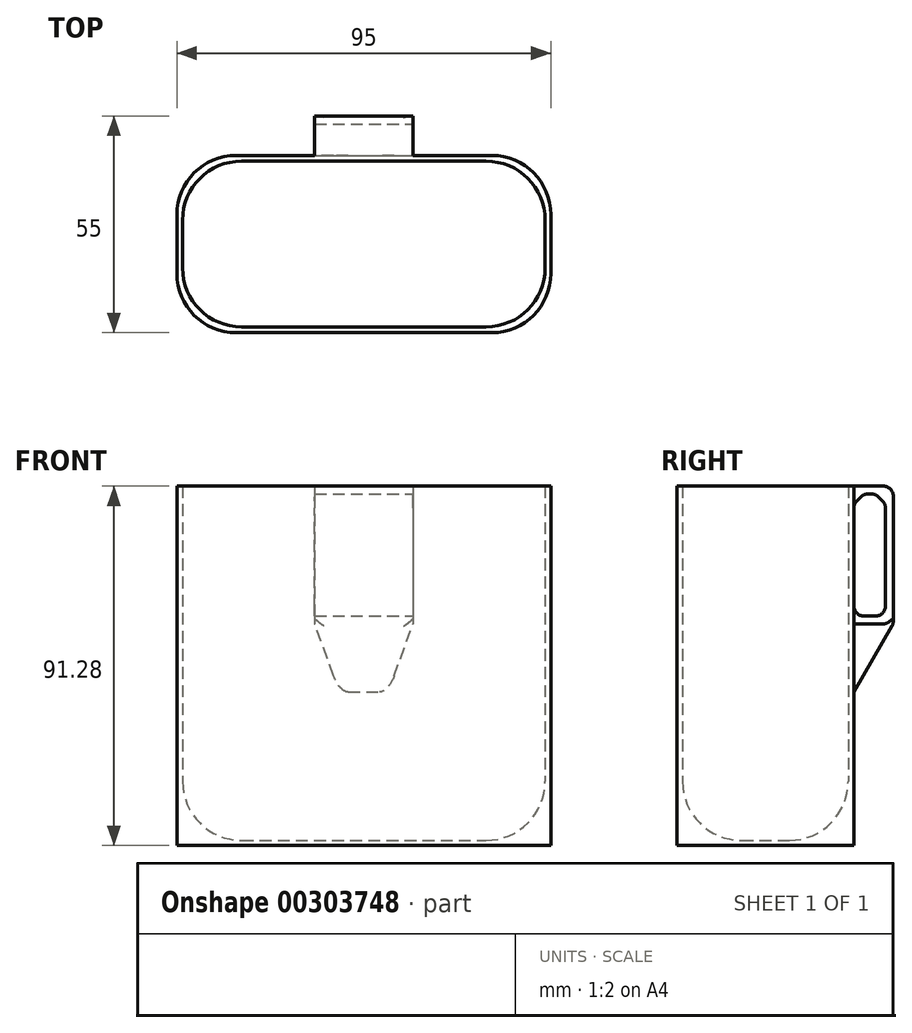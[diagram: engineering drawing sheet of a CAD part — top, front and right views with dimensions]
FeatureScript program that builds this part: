
annotation { "Feature Type Name" : "Feature", "Feature Type Description" : "" }
export const myFeature = defineFeature(function(context is Context, id is Id, definition is map)
    precondition{}
    {
        {
            var Q0;
            Q0=qCreatedBy(makeId("Top.planeOp"),FACE);
            var sketch = newSketch(context, id + "F0", { "sketchPlane" : qUnion([Q0])});
            skLineSegment(sketch, "E0.bottom", {"start": v(0, 0) * mm, "end": v(95, 0) * mm});
            skLineSegment(sketch, "E0.top", {"start": v(0, 45) * mm, "end": v(95, 45) * mm});
            skLineSegment(sketch, "E0.left", {"start": v(0, 0) * mm, "end": v(0, 45) * mm});
            skLineSegment(sketch, "E0.right", {"start": v(95, 0) * mm, "end": v(95, 45) * mm});
            skSolve(sketch);
        }
        {
            var Q0;
            Q0 = qSketchRegion(id + "F0", true);
            extrude(context, id + "F1", {"entities" : qUnion([Q0]), "depth" : (.32 * 4) * mm});
        }
        {
            var Q0;
            Q0=makeQuery(id+"F1.opExtrude","CAP_FACE",FACE,{"disambiguationData":[OSD([sQuery(id+"F0.wireOp",EDGE,"E0.bottom"),sQuery(id+"F0.wireOp",EDGE,"E0.top"),sQuery(id+"F0.wireOp",EDGE,"E0.left"),sQuery(id+"F0.wireOp",EDGE,"E0.right")])],"isStart":false});
            var sketch = newSketch(context, id + "F2", { "sketchPlane" : qUnion([Q0])});
            skLineSegment(sketch, "E1.0.0", {"start": v(95, 45) * mm, "end": v(0, 45) * mm});
            skLineSegment(sketch, "E1.0.1", {"start": v(0, 45) * mm, "end": v(0, 0) * mm});
            skLineSegment(sketch, "E1.0.2", {"start": v(0, 0) * mm, "end": v(95, 0) * mm});
            skLineSegment(sketch, "E1.0.3", {"start": v(95, 0) * mm, "end": v(95, 45) * mm});
            skLineSegment(sketch, "E2.0", {"start": v(93.56, 43.56) * mm, "end": v(1.44, 43.56) * mm});
            skLineSegment(sketch, "E2.1", {"start": v(93.56, 1.44) * mm, "end": v(93.56, 43.56) * mm});
            skLineSegment(sketch, "E2.2", {"start": v(1.44, 1.44) * mm, "end": v(93.56, 1.44) * mm});
            skLineSegment(sketch, "E2.3", {"start": v(1.44, 43.56) * mm, "end": v(1.44, 1.44) * mm});
            skSolve(sketch);
        }
        {
            var Q0;
            Q0 = qSketchRegion(id + "F2", true);
            extrude(context, id + "F3", {"entities" : qUnion([Q0]), "operationType" : NewBodyOperationType.ADD, "depth" : 90 * mm});
        }
        {
            var Q0;
            Q0=makeQuery(id+"F3.boolean.opBoolean","MERGE",FACE,{"derivedFrom":[makeQuery(id+"F1.opExtrude","SWEPT_FACE",FACE,{"disambiguationData":[OSD([sQuery(id+"F0.wireOp",EDGE,"E0.top")])]}),makeQuery(id+"F3.opExtrude","SWEPT_FACE",FACE,{"disambiguationData":[OSD([sQuery(id+"F2.wireOp",EDGE,"E1.0.0")])]})]});
            var sketch = newSketch(context, id + "F4", { "sketchPlane" : qUnion([Q0])});
            skLineSegment(sketch, "E3.bottom", {"start": v(-60, 91.28) * mm, "end": v(-35, 91.28) * mm});
            skLineSegment(sketch, "E3.top", {"start": v(-60, 56.28) * mm, "end": v(-35, 56.28) * mm});
            skLineSegment(sketch, "E3.left", {"start": v(-60, 91.28) * mm, "end": v(-60, 56.28) * mm});
            skLineSegment(sketch, "E3.right", {"start": v(-35, 91.28) * mm, "end": v(-35, 56.28) * mm});
            skSolve(sketch);
        }
        {
            var Q0;
            Q0 = qSketchRegion(id + "F4", true);
            extrude(context, id + "F5", {"entities" : qUnion([Q0]), "operationType" : NewBodyOperationType.ADD, "depth" : 10 * mm});
        }
        {
            var Q0;
            Q0=makeQuery(id+"F5.opExtrude","SWEPT_FACE",FACE,{"disambiguationData":[OSD([sQuery(id+"F4.wireOp",EDGE,"E3.left")])]});
            var sketch = newSketch(context, id + "F6", { "sketchPlane" : qUnion([Q0])});
            skLineSegment(sketch, "E4.0", {"start": v(53, 89.28) * mm, "end": v(45, 89.28) * mm});
            skLineSegment(sketch, "E4.1", {"start": v(53, 89.28) * mm, "end": v(53, 58.28) * mm});
            skLineSegment(sketch, "E4.2", {"start": v(53, 58.28) * mm, "end": v(45, 58.28) * mm});
            skLineSegment(sketch, "E5", {"start": v(45, 89.28) * mm, "end": v(45, 58.28) * mm});
            skSolve(sketch);
        }
        {
            var Q0;
            Q0 = qSketchRegion(id + "F6", true);
            extrude(context, id + "F7", {"entities" : qUnion([Q0]), "operationType" : NewBodyOperationType.REMOVE, "endBound" : BoundingType.THROUGH_ALL, "oppositeDirection" : true, "depth" : 25 * mm});
        }
        {
            var Q0;
            Q0=makeQuery(id+"F5.opExtrude","SWEPT_FACE",FACE,{"disambiguationData":[OSD([sQuery(id+"F4.wireOp",EDGE,"E3.left")])]});
            var sketch = newSketch(context, id + "F8", { "sketchPlane" : qUnion([Q0])});
            skLineSegment(sketch, "E6", {"start": v(45, 56.28) * mm, "end": v(55, 56.28) * mm});
            skLineSegment(sketch, "E7", {"start": v(55, 56.28) * mm, "end": v(45, 38.96) * mm});
            skLineSegment(sketch, "E8", {"start": v(45, 56.28) * mm, "end": v(45, 38.96) * mm});
            skSolve(sketch);
        }
        {
            var Q0;
            Q0 = qSketchRegion(id + "F8", true);
            var Q1;
            Q1=makeQuery(id+"F5.opExtrude","SWEPT_FACE",FACE,{"disambiguationData":[OSD([sQuery(id+"F4.wireOp",EDGE,"E3.right")])]});
            extrude(context, id + "F9", {"entities" : qUnion([Q0]), "operationType" : NewBodyOperationType.ADD, "endBound" : BoundingType.UP_TO_SURFACE, "oppositeDirection" : true, "endBoundEntityFace" : qUnion([Q1]), "depth" : 25 * mm});
        }
        {
            var Q0;
            Q0=makeQuery(id+"F5.opExtrude","CAP_FACE",FACE,{"disambiguationData":[OSD([sQuery(id+"F4.wireOp",EDGE,"E3.bottom"),sQuery(id+"F4.wireOp",EDGE,"E3.top"),sQuery(id+"F4.wireOp",EDGE,"E3.left"),sQuery(id+"F4.wireOp",EDGE,"E3.right")])],"isStart":false});
            var sketch = newSketch(context, id + "F10", { "sketchPlane" : qUnion([Q0])});
            skLineSegment(sketch, "E9.0.2", {"start": v(-60, 56.28) * mm, "end": v(-60, 38.96) * mm});
            skLineSegment(sketch, "E9.0.3", {"start": v(-60, 38.96) * mm, "end": v(-53.7, 38.96) * mm});
            skLineSegment(sketch, "E10", {"start": v(-60, 56.28) * mm, "end": v(-53.7, 38.96) * mm});
            skPoint(sketch, "E9.0.0.end.orphan", {"position": v(-35, 56.28) * mm});
            skPoint(sketch, "E9.0.0.start.orphan", {"position": v(-35, 38.96) * mm});
            skLineSegment(sketch, "E11", {"start": v(-47.5, 56.28) * mm, "end": v(-47.5, 38.96) * mm, "construction": true});
            skLineSegment(sketch, "E12.MirrorCS", {"start": v(-35, 38.96) * mm, "end": v(-41.3, 38.96) * mm});
            skLineSegment(sketch, "E13.MirrorCS", {"start": v(-35, 56.28) * mm, "end": v(-41.3, 38.96) * mm});
            skLineSegment(sketch, "E14.MirrorCS", {"start": v(-35, 56.28) * mm, "end": v(-35, 38.96) * mm});
            skSolve(sketch);
        }
        {
            var Q0;
            Q0 = qSketchRegion(id + "F10", true);
            var Q1;
            Q1=makeQuery(id+"F3.boolean.opBoolean","MERGE",FACE,{"derivedFrom":[makeQuery(id+"F1.opExtrude","SWEPT_FACE",FACE,{"disambiguationData":[OSD([sQuery(id+"F0.wireOp",EDGE,"E0.top")])]}),makeQuery(id+"F3.opExtrude","SWEPT_FACE",FACE,{"disambiguationData":[OSD([sQuery(id+"F2.wireOp",EDGE,"E1.0.0")])]})]});
            extrude(context, id + "F11", {"entities" : qUnion([Q0]), "operationType" : NewBodyOperationType.REMOVE, "endBound" : BoundingType.UP_TO_SURFACE, "oppositeDirection" : true, "endBoundEntityFace" : qUnion([Q1]), "depth" : 25 * mm});
        }
        {
            var Q0;
            Q0=makeQuery(id+"F7.boolean.opBoolean","COPY",EDGE,{"derivedFrom":makeQuery(id+"F7.opExtrude","SWEPT_EDGE",EDGE,{"disambiguationData":[OSD([sQuery(id+"F4.wireOp",EDGE,"E3.left"),sQuery(id+"F6.wireOp",EDGE,"E4.0"),sQuery(id+"F6.wireOp",EDGE,"E5")])]})});
            var Q1;
            Q1=makeQuery(id+"F7.boolean.opBoolean","COPY",EDGE,{"derivedFrom":makeQuery(id+"F7.opExtrude","SWEPT_EDGE",EDGE,{"disambiguationData":[OSD([sQuery(id+"F6.wireOp",EDGE,"E4.0"),sQuery(id+"F6.wireOp",EDGE,"E4.1")])]})});
            chamfer(context, id + "F12", {"entities" : qUnion([Q0, Q1]), "width" : 2.5 * mm, "tangentPropagation" : true});
        }
        {
            var Q0;
            {var subQ0=sQuery(id+"F6.wireOp",EDGE,"E4.0");Q0=makeQuery(id+"F12.opChamfer","BLEND_EDGE",EDGE,{"blendedFrom":[makeQuery(id+"F7.boolean.opBoolean","COPY",EDGE,{"derivedFrom":makeQuery(id+"F7.opExtrude","SWEPT_EDGE",EDGE,{"disambiguationData":[OSD([subQ0,sQuery(id+"F6.wireOp",EDGE,"E4.1")])]})}),makeQuery(id+"F7.boolean.opBoolean","COPY",EDGE,{"derivedFrom":makeQuery(id+"F7.opExtrude","SWEPT_EDGE",EDGE,{"disambiguationData":[OSD([sQuery(id+"F4.wireOp",EDGE,"E3.left"),subQ0,sQuery(id+"F6.wireOp",EDGE,"E5")])]})})],"blendedInto":[]});}
            var Q1;
            {var subQ0=sQuery(id+"F6.wireOp",EDGE,"E5");var subQ1=sQuery(id+"F2.wireOp",EDGE,"E1.0.0");var subQ2=sQuery(id+"F0.wireOp",EDGE,"E0.top");Q1=makeQuery(id+"F12.opChamfer","BLEND_EDGE",EDGE,{"blendedFrom":[makeQuery(id+"F7.boolean.opBoolean","COPY",EDGE,{"derivedFrom":makeQuery(id+"F7.opExtrude","SWEPT_EDGE",EDGE,{"disambiguationData":[OSD([sQuery(id+"F4.wireOp",EDGE,"E3.left"),sQuery(id+"F6.wireOp",EDGE,"E4.0"),subQ0])]})}),makeQuery(id+"F11.boolean.opBoolean","MERGE",FACE,{"derivedFrom":[makeQuery(id+"F7.boolean.opBoolean","MERGE",FACE,{"derivedFrom":[makeQuery(id+"F3.boolean.opBoolean","MERGE",FACE,{"derivedFrom":[makeQuery(id+"F1.opExtrude","SWEPT_FACE",FACE,{"disambiguationData":[OSD([subQ2])]}),makeQuery(id+"F3.opExtrude","SWEPT_FACE",FACE,{"disambiguationData":[OSD([subQ1])]})]}),makeQuery(id+"F7.opExtrude","SWEPT_FACE",FACE,{"disambiguationData":[OSD([subQ0])]})]}),makeQuery(id+"F11.opExtrude","CAP_FACE",FACE,{"disambiguationData":[OSD([subQ2,subQ1,subQ0]),ownerDisambiguation([makeQuery(id+"F11.opExtrude","SWEPT_BODY",BODY,{"disambiguationData":[OSD([sQuery(id+"F10.wireOp",EDGE,"E9.0.2"),sQuery(id+"F10.wireOp",EDGE,"E9.0.3"),sQuery(id+"F10.wireOp",EDGE,"E10")])]})])],"isStart":false}),makeQuery(id+"F11.opExtrude","CAP_FACE",FACE,{"disambiguationData":[OSD([subQ2,subQ1,subQ0]),ownerDisambiguation([makeQuery(id+"F11.opExtrude","SWEPT_BODY",BODY,{"disambiguationData":[OSD([sQuery(id+"F10.wireOp",EDGE,"88048439-b06a-49ce-9c72-6d84dd3895d10.MirrorCS"),sQuery(id+"F10.wireOp",EDGE,"88048439-b06a-49ce-9c72-6d84dd3895d11.MirrorCS"),sQuery(id+"F10.wireOp",EDGE,"88048439-b06a-49ce-9c72-6d84dd3895d12.MirrorCS")])]})])],"isStart":false})]})],"blendedInto":[makeQuery(id+"F11.boolean.opBoolean","MERGE",FACE,{"derivedFrom":[makeQuery(id+"F7.boolean.opBoolean","MERGE",FACE,{"derivedFrom":[makeQuery(id+"F3.boolean.opBoolean","MERGE",FACE,{"derivedFrom":[makeQuery(id+"F1.opExtrude","SWEPT_FACE",FACE,{"disambiguationData":[OSD([subQ2])]}),makeQuery(id+"F3.opExtrude","SWEPT_FACE",FACE,{"disambiguationData":[OSD([subQ1])]})]}),makeQuery(id+"F7.opExtrude","SWEPT_FACE",FACE,{"disambiguationData":[OSD([subQ0])]})]}),makeQuery(id+"F11.opExtrude","CAP_FACE",FACE,{"disambiguationData":[OSD([subQ2,subQ1,subQ0]),ownerDisambiguation([makeQuery(id+"F11.opExtrude","SWEPT_BODY",BODY,{"disambiguationData":[OSD([sQuery(id+"F10.wireOp",EDGE,"E9.0.2"),sQuery(id+"F10.wireOp",EDGE,"E9.0.3"),sQuery(id+"F10.wireOp",EDGE,"E10")])]})])],"isStart":false}),makeQuery(id+"F11.opExtrude","CAP_FACE",FACE,{"disambiguationData":[OSD([subQ2,subQ1,subQ0]),ownerDisambiguation([makeQuery(id+"F11.opExtrude","SWEPT_BODY",BODY,{"disambiguationData":[OSD([sQuery(id+"F10.wireOp",EDGE,"88048439-b06a-49ce-9c72-6d84dd3895d10.MirrorCS"),sQuery(id+"F10.wireOp",EDGE,"88048439-b06a-49ce-9c72-6d84dd3895d11.MirrorCS"),sQuery(id+"F10.wireOp",EDGE,"88048439-b06a-49ce-9c72-6d84dd3895d12.MirrorCS")])]})])],"isStart":false})]})]});}
            var Q2;
            {var subQ0=sQuery(id+"F6.wireOp",EDGE,"E4.1");Q2=makeQuery(id+"F12.opChamfer","BLEND_EDGE",EDGE,{"blendedFrom":[makeQuery(id+"F7.boolean.opBoolean","COPY",EDGE,{"derivedFrom":makeQuery(id+"F7.opExtrude","SWEPT_EDGE",EDGE,{"disambiguationData":[OSD([sQuery(id+"F6.wireOp",EDGE,"E4.0"),subQ0])]})}),makeQuery(id+"F7.boolean.opBoolean","COPY",FACE,{"derivedFrom":makeQuery(id+"F7.opExtrude","SWEPT_FACE",FACE,{"disambiguationData":[OSD([subQ0])]})})],"blendedInto":[makeQuery(id+"F7.boolean.opBoolean","COPY",FACE,{"derivedFrom":makeQuery(id+"F7.opExtrude","SWEPT_FACE",FACE,{"disambiguationData":[OSD([subQ0])]})})]});}
            var Q3;
            Q3=makeQuery(id+"F7.boolean.opBoolean","COPY",EDGE,{"derivedFrom":makeQuery(id+"F7.opExtrude","SWEPT_EDGE",EDGE,{"disambiguationData":[OSD([sQuery(id+"F6.wireOp",EDGE,"E4.1"),sQuery(id+"F6.wireOp",EDGE,"E4.2")])]})});
            var Q4;
            Q4=makeQuery(id+"F7.boolean.opBoolean","COPY",EDGE,{"derivedFrom":makeQuery(id+"F7.opExtrude","SWEPT_EDGE",EDGE,{"disambiguationData":[OSD([sQuery(id+"F4.wireOp",EDGE,"E3.left"),sQuery(id+"F6.wireOp",EDGE,"E4.2"),sQuery(id+"F6.wireOp",EDGE,"E5")])]})});
            var Q5;
            Q5=makeQuery(id+"F5.opExtrude","CAP_EDGE",EDGE,{"disambiguationData":[OSD([sQuery(id+"F4.wireOp",EDGE,"E3.bottom")])],"isStart":false});
            var Q6;
            Q6=makeQuery(id+"F9.boolean.opBoolean","MERGE",EDGE,{"derivedFrom":[makeQuery(id+"F5.opExtrude","CAP_EDGE",EDGE,{"disambiguationData":[OSD([sQuery(id+"F4.wireOp",EDGE,"E3.top")])],"isStart":false}),makeQuery(id+"F9.opExtrude","SWEPT_EDGE",EDGE,{"disambiguationData":[OSD([sQuery(id+"F4.wireOp",EDGE,"E3.left"),sQuery(id+"F8.wireOp",EDGE,"E6"),sQuery(id+"F8.wireOp",EDGE,"E7")])]})]});
            var Q7;
            Q7=makeQuery(id+"F11.boolean.opBoolean","INTERSECT",EDGE,{"derivedFrom":[makeQuery(id+"F9.opExtrude","SWEPT_FACE",FACE,{"disambiguationData":[OSD([sQuery(id+"F8.wireOp",EDGE,"E7")])]}),makeQuery(id+"F11.opExtrude","SWEPT_FACE",FACE,{"disambiguationData":[OSD([sQuery(id+"F10.wireOp",EDGE,"E10")])]})]});
            var Q8;
            Q8=makeQuery(id+"F11.boolean.opBoolean","INTERSECT",EDGE,{"derivedFrom":[makeQuery(id+"F9.opExtrude","SWEPT_FACE",FACE,{"disambiguationData":[OSD([sQuery(id+"F8.wireOp",EDGE,"E7")])]}),makeQuery(id+"F11.opExtrude","SWEPT_FACE",FACE,{"disambiguationData":[OSD([sQuery(id+"F10.wireOp",EDGE,"E13.MirrorCS")])]})]});
            var Q9;
            {var subQ0=sQuery(id+"F6.wireOp",EDGE,"E4.0");Q9=makeQuery(id+"F12.opChamfer","BLEND_EDGE",EDGE,{"blendedFrom":[makeQuery(id+"F7.boolean.opBoolean","COPY",EDGE,{"derivedFrom":makeQuery(id+"F7.opExtrude","SWEPT_EDGE",EDGE,{"disambiguationData":[OSD([sQuery(id+"F4.wireOp",EDGE,"E3.left"),subQ0,sQuery(id+"F6.wireOp",EDGE,"E5")])]})}),makeQuery(id+"F7.boolean.opBoolean","COPY",FACE,{"derivedFrom":makeQuery(id+"F7.opExtrude","SWEPT_FACE",FACE,{"disambiguationData":[OSD([subQ0])]})})],"blendedInto":[makeQuery(id+"F7.boolean.opBoolean","COPY",FACE,{"derivedFrom":makeQuery(id+"F7.opExtrude","SWEPT_FACE",FACE,{"disambiguationData":[OSD([subQ0])]})})]});}
            var Q10;
            {var subQ0=sQuery(id+"F6.wireOp",EDGE,"E4.0");Q10=makeQuery(id+"F12.opChamfer","BLEND_EDGE",EDGE,{"blendedFrom":[makeQuery(id+"F7.boolean.opBoolean","COPY",EDGE,{"derivedFrom":makeQuery(id+"F7.opExtrude","SWEPT_EDGE",EDGE,{"disambiguationData":[OSD([subQ0,sQuery(id+"F6.wireOp",EDGE,"E4.1")])]})}),makeQuery(id+"F7.boolean.opBoolean","COPY",FACE,{"derivedFrom":makeQuery(id+"F7.opExtrude","SWEPT_FACE",FACE,{"disambiguationData":[OSD([subQ0])]})})],"blendedInto":[makeQuery(id+"F7.boolean.opBoolean","COPY",FACE,{"derivedFrom":makeQuery(id+"F7.opExtrude","SWEPT_FACE",FACE,{"disambiguationData":[OSD([subQ0])]})})]});}
            fillet(context, id + "F13", {"entities" : qUnion([Q0, Q1, Q2, Q3, Q4, Q5, Q6, Q7, Q8, Q9, Q10]), "radius" : 2.5 * mm, "tangentPropagation" : true, "allowEdgeOverflow" : false});
        }
        {
            var Q0;
            Q0=makeQuery(id+"F3.opExtrude","SWEPT_EDGE",EDGE,{"disambiguationData":[OSD([sQuery(id+"F2.wireOp",EDGE,"E2.0"),sQuery(id+"F2.wireOp",EDGE,"E2.3")])]});
            var Q1;
            Q1=makeQuery(id+"F3.opExtrude","SWEPT_EDGE",EDGE,{"disambiguationData":[OSD([sQuery(id+"F2.wireOp",EDGE,"E2.2"),sQuery(id+"F2.wireOp",EDGE,"E2.3")])]});
            var Q2;
            Q2=makeQuery(id+"F3.opExtrude","SWEPT_EDGE",EDGE,{"disambiguationData":[OSD([sQuery(id+"F2.wireOp",EDGE,"E2.0"),sQuery(id+"F2.wireOp",EDGE,"E2.1")])]});
            var Q3;
            Q3=makeQuery(id+"F3.opExtrude","SWEPT_EDGE",EDGE,{"disambiguationData":[OSD([sQuery(id+"F2.wireOp",EDGE,"E2.1"),sQuery(id+"F2.wireOp",EDGE,"E2.2")])]});
            fillet(context, id + "F14", {"entities" : qUnion([Q0, Q1, Q2, Q3]), "radius" : 15 * mm, "tangentPropagation" : true, "allowEdgeOverflow" : false});
        }
        {
            var Q0;
            Q0=makeQuery(id+"F3.boolean.opBoolean","MERGE",EDGE,{"derivedFrom":[makeQuery(id+"F1.opExtrude","SWEPT_EDGE",EDGE,{"disambiguationData":[OSD([sQuery(id+"F0.wireOp",EDGE,"E0.bottom"),sQuery(id+"F0.wireOp",EDGE,"E0.right")])]}),makeQuery(id+"F3.opExtrude","SWEPT_EDGE",EDGE,{"disambiguationData":[OSD([sQuery(id+"F2.wireOp",EDGE,"E1.0.2"),sQuery(id+"F2.wireOp",EDGE,"E1.0.3")])]})]});
            var Q1;
            Q1=makeQuery(id+"F3.boolean.opBoolean","MERGE",EDGE,{"derivedFrom":[makeQuery(id+"F1.opExtrude","SWEPT_EDGE",EDGE,{"disambiguationData":[OSD([sQuery(id+"F0.wireOp",EDGE,"E0.top"),sQuery(id+"F0.wireOp",EDGE,"E0.right")])]}),makeQuery(id+"F3.opExtrude","SWEPT_EDGE",EDGE,{"disambiguationData":[OSD([sQuery(id+"F2.wireOp",EDGE,"E1.0.0"),sQuery(id+"F2.wireOp",EDGE,"E1.0.3")])]})]});
            var Q2;
            Q2=makeQuery(id+"F3.boolean.opBoolean","MERGE",EDGE,{"derivedFrom":[makeQuery(id+"F1.opExtrude","SWEPT_EDGE",EDGE,{"disambiguationData":[OSD([sQuery(id+"F0.wireOp",EDGE,"E0.top"),sQuery(id+"F0.wireOp",EDGE,"E0.left")])]}),makeQuery(id+"F3.opExtrude","SWEPT_EDGE",EDGE,{"disambiguationData":[OSD([sQuery(id+"F2.wireOp",EDGE,"E1.0.0"),sQuery(id+"F2.wireOp",EDGE,"E1.0.1")])]})]});
            var Q3;
            Q3=makeQuery(id+"F3.boolean.opBoolean","MERGE",EDGE,{"derivedFrom":[makeQuery(id+"F1.opExtrude","SWEPT_EDGE",EDGE,{"disambiguationData":[OSD([sQuery(id+"F0.wireOp",EDGE,"E0.bottom"),sQuery(id+"F0.wireOp",EDGE,"E0.left")])]}),makeQuery(id+"F3.opExtrude","SWEPT_EDGE",EDGE,{"disambiguationData":[OSD([sQuery(id+"F2.wireOp",EDGE,"E1.0.1"),sQuery(id+"F2.wireOp",EDGE,"E1.0.2")])]})]});
            fillet(context, id + "F15", {"entities" : qUnion([Q0, Q1, Q2, Q3]), "radius" : 15 * mm, "tangentPropagation" : true, "allowEdgeOverflow" : false});
        }
        {
            var Q0;
            Q0=makeQuery(id+"F1.opExtrude","CAP_FACE",FACE,{"disambiguationData":[OSD([sQuery(id+"F0.wireOp",EDGE,"E0.bottom"),sQuery(id+"F0.wireOp",EDGE,"E0.top"),sQuery(id+"F0.wireOp",EDGE,"E0.left"),sQuery(id+"F0.wireOp",EDGE,"E0.right")])],"isStart":false});
            fillet(context, id + "F16", {"entities" : qUnion([Q0]), "radius" : 15 * mm, "tangentPropagation" : true, "allowEdgeOverflow" : false});
        }
    });
